# Revit family: Fireplace_Gas_HeatNGlo_8000-6000-Modern
name_source: partatom
category: Mechanical Equipment
revit_build: Autodesk Revit 2015 (Build: 20140323_1530(x64)
units: mm (PartAtom-declared; Revit-internal decimal feet)

## types (4) — shared parameters
Assembly Code = D3020
Construction Details = http://www.arcat.com
Default Elevation = 0' - 0"
Fuel Consumption = as Specified
HVAC_BTU Output = 0.0 Btu/h
Heating Capacity = as Specified
Keynote = 10305
Manufacturer = Heat & Glo
Manufacturer Website = http://www.heatnglo.com
Product Data = http://www.arcat.com
Revision = R1_06_2014
Sales Information = http://www.heatnglo.com
Send Message = http://www.arcat.com
Specification = http://www.arcat.com
Standards Conformance = cULus
URL = http://www.heatnglo.com
Unit Depth = 1' - 9"
zero-valued in all types: Expected Lifespan (Years), Maintenance Schedule (Months), Unit Weight, Warranty Duration (Years)

## per-type parameters (varying)
| type | Description | Efficiency Ratings | Fuel Type | HVAC_BTU Input | Model | Opening Height | Opening Width | Rear Width | Unit Height | Unit Width |
| 43x26 Viewing Area LP | Heat & Glo Gas Burning Fireplace - 8000 Modern 8000CMOD-IPI as Specified | Steady State: 77.5  ;  AFUE: 55.9  ;  EnerGuide: 61.7 | LP | 22000.0 Btu/h | 8000CMOD-IPI | 2' - 1 5/8" | 3' - 7 1/8" | 2' - 11 1/2" | 3' - 6 7/8" | 4' - 0" |
| 43x26 Viewing Area NG | Heat & Glo Gas Burning Fireplace - 8000 Modern 8000CMOD-IPI as Specified | Steady State: 77.5  ;  AFUE: 55.9  ;  EnerGuide: 61.7 | NG | 32000.0 Btu/h | 8000CMOD-IPI | 2' - 1 5/8" | 3' - 7 1/8" | 2' - 11 1/2" | 3' - 6 7/8" | 4' - 0" |
| 36x24 Viewing Area LP | Heat & Glo Gas Burning Fireplace - 6000 Modern 6000CMOD-IPI as Specified | Steady State: 78.5  ;  AFUE: 61.1  ;  EnerGuide: 63 | LP | 20000.0 Btu/h | 6000CMOD-IPI | 1' - 11 5/8" | 3' - 0 1/8" | 2' - 4 1/2" | 3' - 4 7/8" | 3' - 5" |
| 36x24 Viewing Area NG | Heat & Glo Gas Burning Fireplace - 6000 Modern 6000CMOD-IPI as Specified | Steady State: 78.5  ;  AFUE: 61.1  ;  EnerGuide: 63 | NG | 28000.0 Btu/h | 6000CMOD-IPI | 1' - 11 5/8" | 3' - 0 1/8" | 2' - 4 1/2" | 3' - 4 7/8" | 3' - 5" |

## geometry (parser evidence)
native form markers: Blend x8, Sweep x6
no freeform markers — native parametric forms only
